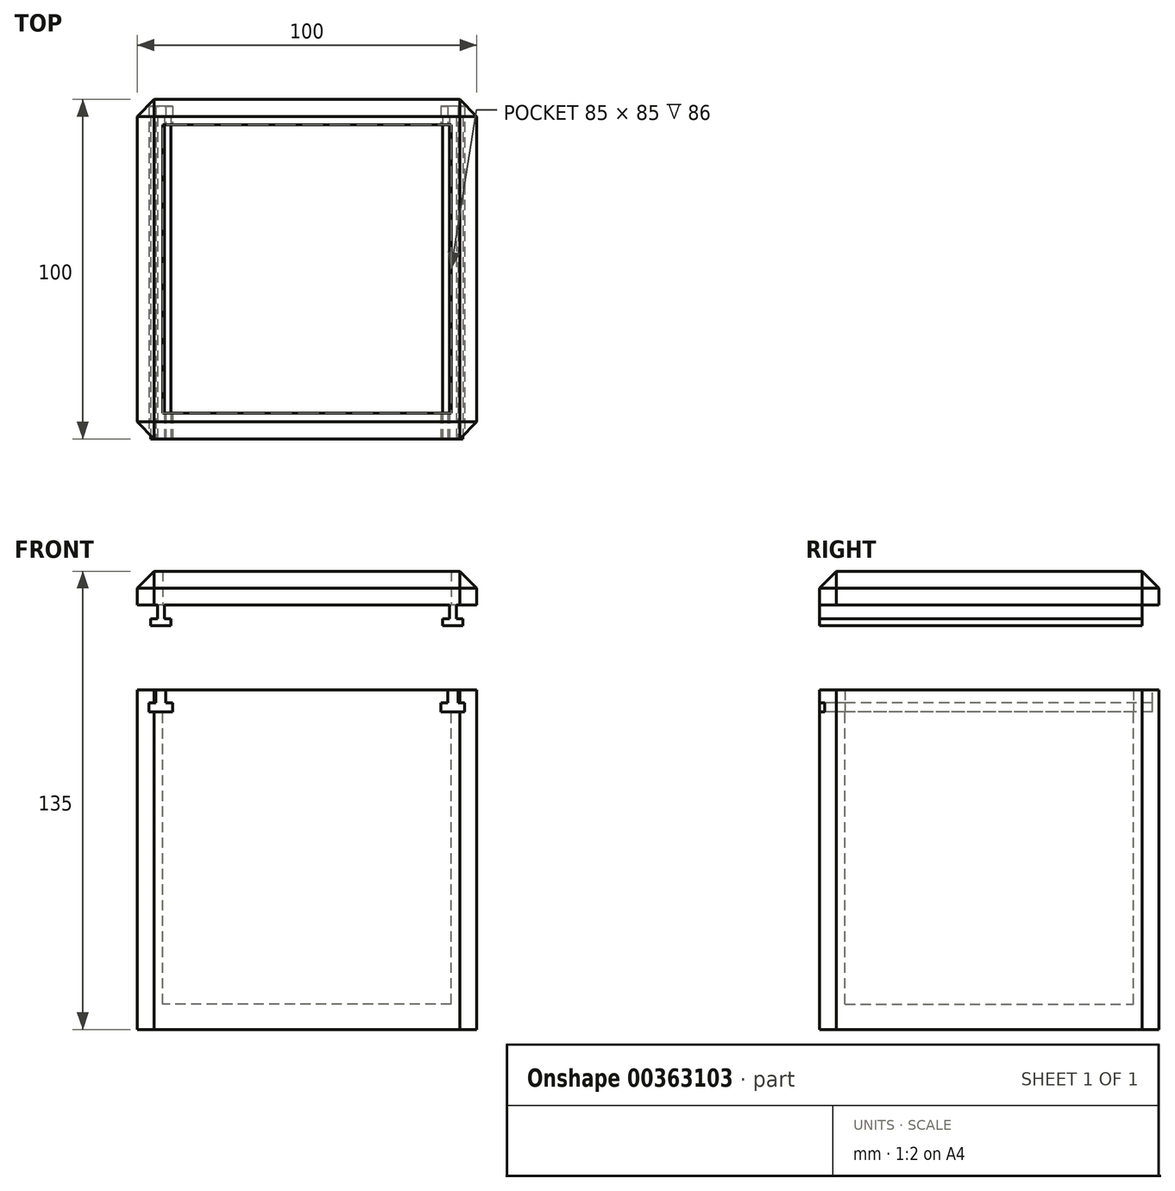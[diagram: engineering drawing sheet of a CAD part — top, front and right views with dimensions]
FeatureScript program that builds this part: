
annotation { "Feature Type Name" : "Feature", "Feature Type Description" : "" }
export const myFeature = defineFeature(function(context is Context, id is Id, definition is map)
    precondition{}
    {
        {
            var Q0;
            Q0=qCreatedBy(makeId("Front.planeOp"),FACE);
            var sketch = newSketch(context, id + "F0", { "sketchPlane" : qUnion([Q0])});
            skLineSegment(sketch, "E0.bottom", {"start": v(50, 50) * mm, "end": v(-50, 50) * mm});
            skLineSegment(sketch, "E0.top", {"start": v(50, -50) * mm, "end": v(-50, -50) * mm});
            skLineSegment(sketch, "E0.left", {"start": v(50, 50) * mm, "end": v(50, -50) * mm});
            skLineSegment(sketch, "E0.right", {"start": v(-50, 50) * mm, "end": v(-50, -50) * mm});
            skPoint(sketch, "E0.middle", {"position": v(0, 0) * mm});
            skLineSegment(sketch, "E1.bottom", {"start": v(42.5, 42.5) * mm, "end": v(-42.5, 42.5) * mm});
            skLineSegment(sketch, "E1.top", {"start": v(42.5, -42.5) * mm, "end": v(-42.5, -42.5) * mm});
            skLineSegment(sketch, "E1.left", {"start": v(42.5, 42.5) * mm, "end": v(42.5, -42.5) * mm});
            skLineSegment(sketch, "E1.right", {"start": v(-42.5, 42.5) * mm, "end": v(-42.5, -42.5) * mm});
            skSolve(sketch);
        }
        {
            var Q0;
            Q0=qCreatedBy(makeId("Right.planeOp"),FACE);
            var sketch = newSketch(context, id + "F1", { "sketchPlane" : qUnion([Q0])});
            skLineSegment(sketch, "E2.bottom", {"start": v(50, 50) * mm, "end": v(-50, 50) * mm});
            skLineSegment(sketch, "E2.top", {"start": v(50, -50) * mm, "end": v(-50, -50) * mm});
            skLineSegment(sketch, "E2.left", {"start": v(50, 50) * mm, "end": v(50, -50) * mm});
            skLineSegment(sketch, "E2.right", {"start": v(-50, 50) * mm, "end": v(-50, -50) * mm});
            skPoint(sketch, "E2.middle", {"position": v(0, 0) * mm});
            skLineSegment(sketch, "E3.bottom", {"start": v(42.5, 42.5) * mm, "end": v(-42.5, 42.5) * mm});
            skLineSegment(sketch, "E3.top", {"start": v(42.5, -42.5) * mm, "end": v(-42.5, -42.5) * mm});
            skLineSegment(sketch, "E3.left", {"start": v(42.5, 42.5) * mm, "end": v(42.5, -42.5) * mm});
            skLineSegment(sketch, "E3.right", {"start": v(-42.5, 42.5) * mm, "end": v(-42.5, -42.5) * mm});
            skSolve(sketch);
        }
        {
            var Q0;
            Q0=makeQuery(id+"F0.imprint","IMPRINT",FACE,{"disambiguationData":[TD([[makeQuery(id+"F0.imprint","IMPRINT",EDGE,{"derivedFrom":sQuery(id+"F0.wireOp",EDGE,"E0.bottom")}),1.0]])]});
            extrude(context, id + "F2", {"entities" : qUnion([Q0]), "endBound" : BoundingType.SYMMETRIC, "depth" : 100 * mm});
        }
        {
            var Q0;
            Q0=makeQuery(id+"F1.imprint","IMPRINT",FACE,{"disambiguationData":[TD([[makeQuery(id+"F1.imprint","IMPRINT",EDGE,{"derivedFrom":sQuery(id+"F1.wireOp",EDGE,"E2.bottom")}),1.0]])]});
            extrude(context, id + "F3", {"entities" : qUnion([Q0]), "operationType" : NewBodyOperationType.ADD, "endBound" : BoundingType.SYMMETRIC, "depth" : 100 * mm});
        }
        {
            var Q0;
            {var subQ7=sQuery(id+"F0.wireOp",EDGE,"E1.right");var subQ8=sQuery(id+"F0.wireOp",EDGE,"E1.bottom");var subQ9=makeQuery(id+"F0.imprint","INTERSECT",VERTEX,{"derivedFrom":[subQ8,subQ7]});Q0=makeQuery(id+"F0.imprint","IMPRINT",FACE,{"disambiguationData":[TD([[makeQuery(id+"F0.imprint","IMPRINT",EDGE,{"disambiguationData":[TD([[subQ9,1.0]])],"derivedFrom":subQ8}),1.0]])]});}
            var Q1;
            {var subQ0=sQuery(id+"F0.wireOp",EDGE,"E1.right");var subQ1=sQuery(id+"F0.wireOp",EDGE,"E1.top");var subQ2=makeQuery(id+"F0.imprint","INTERSECT",VERTEX,{"derivedFrom":[subQ1,subQ0]});Q1=makeQuery(id+"F0.imprint","IMPRINT",FACE,{"disambiguationData":[TD([[makeQuery(id+"F0.imprint","IMPRINT",EDGE,{"disambiguationData":[TD([[subQ2,1.0]])],"derivedFrom":subQ1}),-1.0]])]});}
            var Q2;
            {var subQ0=sQuery(id+"F0.wireOp",EDGE,"E1.left");var subQ1=sQuery(id+"F0.wireOp",EDGE,"E1.bottom");var subQ2=makeQuery(id+"F0.imprint","INTERSECT",VERTEX,{"derivedFrom":[subQ1,subQ0]});Q2=makeQuery(id+"F0.imprint","IMPRINT",FACE,{"disambiguationData":[TD([[makeQuery(id+"F0.imprint","IMPRINT",EDGE,{"disambiguationData":[TD([[subQ2,-1.0]])],"derivedFrom":subQ1}),1.0]])]});}
            extrude(context, id + "F4", {"entities" : qUnion([Q0, Q1, Q2]), "operationType" : NewBodyOperationType.REMOVE, "endBound" : BoundingType.SYMMETRIC, "oppositeDirection" : true, "depth" : 85 * mm});
        }
        {
            var Q0;
            Q0=qCreatedBy(makeId("Top.planeOp"),FACE);
            var sketch = newSketch(context, id + "F5", { "sketchPlane" : qUnion([Q0])});
            skLineSegment(sketch, "E4.bottom", {"start": v(42.5, 42.5) * mm, "end": v(-42.5, 42.5) * mm});
            skLineSegment(sketch, "E4.top", {"start": v(42.5, -42.5) * mm, "end": v(-42.5, -42.5) * mm});
            skLineSegment(sketch, "E4.left", {"start": v(42.5, 42.5) * mm, "end": v(42.5, -42.5) * mm});
            skLineSegment(sketch, "E4.right", {"start": v(-42.5, 42.5) * mm, "end": v(-42.5, -42.5) * mm});
            skPoint(sketch, "E4.middle", {"position": v(0, 0) * mm});
            skSolve(sketch);
        }
        {
            var Q0;
            Q0=makeQuery(id+"F2.opExtrude","SWEPT_FACE",FACE,{"disambiguationData":[OSD([sQuery(id+"F0.wireOp",EDGE,"E0.bottom")])]});
            var sketch = newSketch(context, id + "F6", { "sketchPlane" : qUnion([Q0])});
            skLineSegment(sketch, "E5.bottom", {"start": v(50, -50) * mm, "end": v(-50, -50) * mm});
            skLineSegment(sketch, "E5.top", {"start": v(50, 50) * mm, "end": v(-50, 50) * mm});
            skLineSegment(sketch, "E5.left", {"start": v(50, -50) * mm, "end": v(50, 50) * mm});
            skLineSegment(sketch, "E5.right", {"start": v(-50, -50) * mm, "end": v(-50, 50) * mm});
            skPoint(sketch, "E5.middle", {"position": v(0, 0) * mm});
            skSolve(sketch);
        }
        {
            var Q0;
            Q0=makeQuery(id+"F6.imprint","IMPRINT",FACE,{"disambiguationData":[TD([[makeQuery(id+"F6.imprint","IMPRINT",EDGE,{"derivedFrom":sQuery(id+"F6.wireOp",EDGE,"E5.bottom")}),-1.0]])]});
            extrude(context, id + "F7", {"entities" : qUnion([Q0]), "depth" : 10 * mm});
        }
        {
            var Q0;
            Q0 = qSketchRegion(id + "F5", true);
            extrude(context, id + "F8", {"entities" : qUnion([Q0]), "operationType" : NewBodyOperationType.REMOVE, "depth" : 120 * mm});
        }
        {
            var Q0;
            Q0=makeQuery(id+"F7.opExtrude","SWEPT_FACE",FACE,{"disambiguationData":[OSD([sQuery(id+"F6.wireOp",EDGE,"E5.bottom")])]});
            var sketch = newSketch(context, id + "F9", { "sketchPlane" : qUnion([Q0])});
            skLineSegment(sketch, "E6", {"start": v(-44, 50) * mm, "end": v(-44, 46) * mm});
            skLineSegment(sketch, "E7", {"start": v(-44, 46) * mm, "end": v(-46, 46) * mm});
            skLineSegment(sketch, "E8", {"start": v(-46, 46) * mm, "end": v(-46, 44) * mm});
            skLineSegment(sketch, "E9", {"start": v(-46, 44) * mm, "end": v(-40, 44) * mm});
            skLineSegment(sketch, "E10", {"start": v(-40, 44) * mm, "end": v(-40, 46) * mm});
            skLineSegment(sketch, "E11", {"start": v(-40, 46) * mm, "end": v(-42, 46) * mm});
            skLineSegment(sketch, "E12", {"start": v(-42, 46) * mm, "end": v(-42, 50) * mm});
            skLineSegment(sketch, "E13.MirrorCS", {"start": v(46, 44) * mm, "end": v(40, 44) * mm});
            skLineSegment(sketch, "E14.MirrorCS", {"start": v(44, 50) * mm, "end": v(44, 46) * mm});
            skLineSegment(sketch, "E15.MirrorCS", {"start": v(42, 46) * mm, "end": v(42, 50) * mm});
            skLineSegment(sketch, "E16.MirrorCS", {"start": v(40, 46) * mm, "end": v(42, 46) * mm});
            skLineSegment(sketch, "E17.MirrorCS", {"start": v(40, 44) * mm, "end": v(40, 46) * mm});
            skLineSegment(sketch, "E18.MirrorCS", {"start": v(46, 46) * mm, "end": v(46, 44) * mm});
            skLineSegment(sketch, "E19.MirrorCS", {"start": v(44, 46) * mm, "end": v(46, 46) * mm});
            skSolve(sketch);
        }
        {
            var Q0;
            Q0=makeQuery(id+"F3.boolean.opBoolean","MERGE",FACE,{"derivedFrom":[makeQuery(id+"F2.opExtrude","CAP_FACE",FACE,{"disambiguationData":[OSD([sQuery(id+"F0.wireOp",EDGE,"E0.bottom"),sQuery(id+"F0.wireOp",EDGE,"E0.top"),sQuery(id+"F0.wireOp",EDGE,"E0.left"),sQuery(id+"F0.wireOp",EDGE,"E0.right"),sQuery(id+"F0.wireOp",EDGE,"E1.bottom"),sQuery(id+"F0.wireOp",EDGE,"E1.top"),sQuery(id+"F0.wireOp",EDGE,"E1.left"),sQuery(id+"F0.wireOp",EDGE,"E1.right")])],"isStart":false}),makeQuery(id+"F3.opExtrude","SWEPT_FACE",FACE,{"disambiguationData":[OSD([sQuery(id+"F1.wireOp",EDGE,"E2.right")])]})]});
            var sketch = newSketch(context, id + "F10", { "sketchPlane" : qUnion([Q0])});
            skLineSegment(sketch, "E20", {"start": v(-44.5, 50) * mm, "end": v(-44.5, 46.25) * mm});
            skLineSegment(sketch, "E21", {"start": v(-44.5, 46.25) * mm, "end": v(-46.5, 46.25) * mm});
            skLineSegment(sketch, "E22", {"start": v(-46.5, 46.25) * mm, "end": v(-46.5, 43.5) * mm});
            skLineSegment(sketch, "E23", {"start": v(-46.5, 43.5) * mm, "end": v(-39.5, 43.5) * mm});
            skLineSegment(sketch, "E24", {"start": v(-39.5, 43.5) * mm, "end": v(-39.5, 46.25) * mm});
            skLineSegment(sketch, "E25", {"start": v(-39.5, 46.25) * mm, "end": v(-41.5, 46.25) * mm});
            skLineSegment(sketch, "E26", {"start": v(-41.5, 46.25) * mm, "end": v(-41.5, 50) * mm});
            skLineSegment(sketch, "E27.MirrorCS", {"start": v(46.5, 43.5) * mm, "end": v(39.5, 43.5) * mm});
            skLineSegment(sketch, "E28.MirrorCS", {"start": v(46.5, 46.25) * mm, "end": v(46.5, 43.5) * mm});
            skLineSegment(sketch, "E29.MirrorCS", {"start": v(44.5, 46.25) * mm, "end": v(46.5, 46.25) * mm});
            skLineSegment(sketch, "E30.MirrorCS", {"start": v(44.5, 50) * mm, "end": v(44.5, 46.25) * mm});
            skLineSegment(sketch, "E31.MirrorCS", {"start": v(41.5, 46.25) * mm, "end": v(41.5, 50) * mm});
            skLineSegment(sketch, "E32.MirrorCS", {"start": v(39.5, 46.25) * mm, "end": v(41.5, 46.25) * mm});
            skLineSegment(sketch, "E33.MirrorCS", {"start": v(39.5, 43.5) * mm, "end": v(39.5, 46.25) * mm});
            skSolve(sketch);
        }
        {
            var Q0;
            {var subQ0=sQuery(id+"F10.wireOp",EDGE,"E20");Q0=makeQuery(id+"F10.imprint","IMPRINT",FACE,{"disambiguationData":[TD([[makeQuery(id+"F10.imprint","IMPRINT",EDGE,{"derivedFrom":subQ0}),1.0]])]});}
            var Q1;
            Q1=makeQuery(id+"F10.imprint","IMPRINT",FACE,{"disambiguationData":[TD([[makeQuery(id+"F10.imprint","IMPRINT",EDGE,{"derivedFrom":sQuery(id+"F10.wireOp",EDGE,"E27.MirrorCS")}),-1.0]])]});
            extrude(context, id + "F11", {"entities" : qUnion([Q0, Q1]), "operationType" : NewBodyOperationType.REMOVE, "oppositeDirection" : true, "depth" : 98 * mm});
        }
        {
            var Q0;
            {var subQ0=sQuery(id+"F9.wireOp",EDGE,"E6");Q0=makeQuery(id+"F9.imprint","IMPRINT",FACE,{"disambiguationData":[TD([[makeQuery(id+"F9.imprint","IMPRINT",EDGE,{"derivedFrom":subQ0}),1.0]])]});}
            var Q1;
            Q1=makeQuery(id+"F9.imprint","IMPRINT",FACE,{"disambiguationData":[TD([[makeQuery(id+"F9.imprint","IMPRINT",EDGE,{"derivedFrom":sQuery(id+"F9.wireOp",EDGE,"E13.MirrorCS")}),-1.0]])]});
            extrude(context, id + "F12", {"entities" : qUnion([Q0, Q1]), "operationType" : NewBodyOperationType.ADD, "oppositeDirection" : true, "depth" : 95 * mm});
        }
        {
            var Q0;
            Q0=makeQuery(id+"F7.opExtrude","SWEPT_BODY",BODY,{"disambiguationData":[OSD([sQuery(id+"F6.wireOp",EDGE,"E5.bottom"),sQuery(id+"F6.wireOp",EDGE,"E5.top"),sQuery(id+"F6.wireOp",EDGE,"E5.left"),sQuery(id+"F6.wireOp",EDGE,"E5.right")])]});
            transform(context, id + "F13", {"entities" : qUnion([Q0]), "transformType" : TransformType.TRANSLATION_3D, "dx" : 0 * mm, "dy" : 0 * mm, "dz" : 25 * mm, "makeCopy" : false});
        }
        {
            var Q0;
            Q0=makeQuery(id+"F7.opExtrude","CAP_EDGE",EDGE,{"disambiguationData":[OSD([sQuery(id+"F6.wireOp",EDGE,"E5.bottom")])],"isStart":false});
            var Q1;
            Q1=makeQuery(id+"F7.opExtrude","CAP_EDGE",EDGE,{"disambiguationData":[OSD([sQuery(id+"F6.wireOp",EDGE,"E5.left")])],"isStart":false});
            var Q2;
            Q2=makeQuery(id+"F7.opExtrude","CAP_EDGE",EDGE,{"disambiguationData":[OSD([sQuery(id+"F6.wireOp",EDGE,"E5.top")])],"isStart":false});
            var Q3;
            Q3=makeQuery(id+"F7.opExtrude","CAP_EDGE",EDGE,{"disambiguationData":[OSD([sQuery(id+"F6.wireOp",EDGE,"E5.right")])],"isStart":false});
            var Q4;
            Q4=makeQuery(id+"F7.opExtrude","SWEPT_EDGE",EDGE,{"disambiguationData":[OSD([sQuery(id+"F6.wireOp",EDGE,"E5.bottom"),sQuery(id+"F6.wireOp",EDGE,"E5.left")])]});
            var Q5;
            Q5=makeQuery(id+"F7.opExtrude","SWEPT_EDGE",EDGE,{"disambiguationData":[OSD([sQuery(id+"F6.wireOp",EDGE,"E5.top"),sQuery(id+"F6.wireOp",EDGE,"E5.left")])]});
            var Q6;
            Q6=makeQuery(id+"F7.opExtrude","SWEPT_EDGE",EDGE,{"disambiguationData":[OSD([sQuery(id+"F6.wireOp",EDGE,"E5.top"),sQuery(id+"F6.wireOp",EDGE,"E5.right")])]});
            var Q7;
            Q7=makeQuery(id+"F7.opExtrude","SWEPT_EDGE",EDGE,{"disambiguationData":[OSD([sQuery(id+"F6.wireOp",EDGE,"E5.bottom"),sQuery(id+"F6.wireOp",EDGE,"E5.right")])]});
            chamfer(context, id + "F14", {"entities" : qUnion([Q0, Q1, Q2, Q3, Q4, Q5, Q6, Q7]), "width" : 5 * mm, "tangentPropagation" : true});
        }
        {
            var Q0;
            Q0=makeQuery(id+"F2.opExtrude","CAP_EDGE",EDGE,{"disambiguationData":[OSD([sQuery(id+"F0.wireOp",EDGE,"E0.left")])],"isStart":false});
            var Q1;
            Q1=makeQuery(id+"F2.opExtrude","CAP_EDGE",EDGE,{"disambiguationData":[OSD([sQuery(id+"F0.wireOp",EDGE,"E0.left")])],"isStart":true});
            var Q2;
            Q2=makeQuery(id+"F2.opExtrude","CAP_EDGE",EDGE,{"disambiguationData":[OSD([sQuery(id+"F0.wireOp",EDGE,"E0.right")])],"isStart":true});
            var Q3;
            Q3=makeQuery(id+"F2.opExtrude","CAP_EDGE",EDGE,{"disambiguationData":[OSD([sQuery(id+"F0.wireOp",EDGE,"E0.right")])],"isStart":false});
            chamfer(context, id + "F15", {"entities" : qUnion([Q0, Q1, Q2, Q3]), "width" : 5 * mm, "tangentPropagation" : true});
        }
    });
